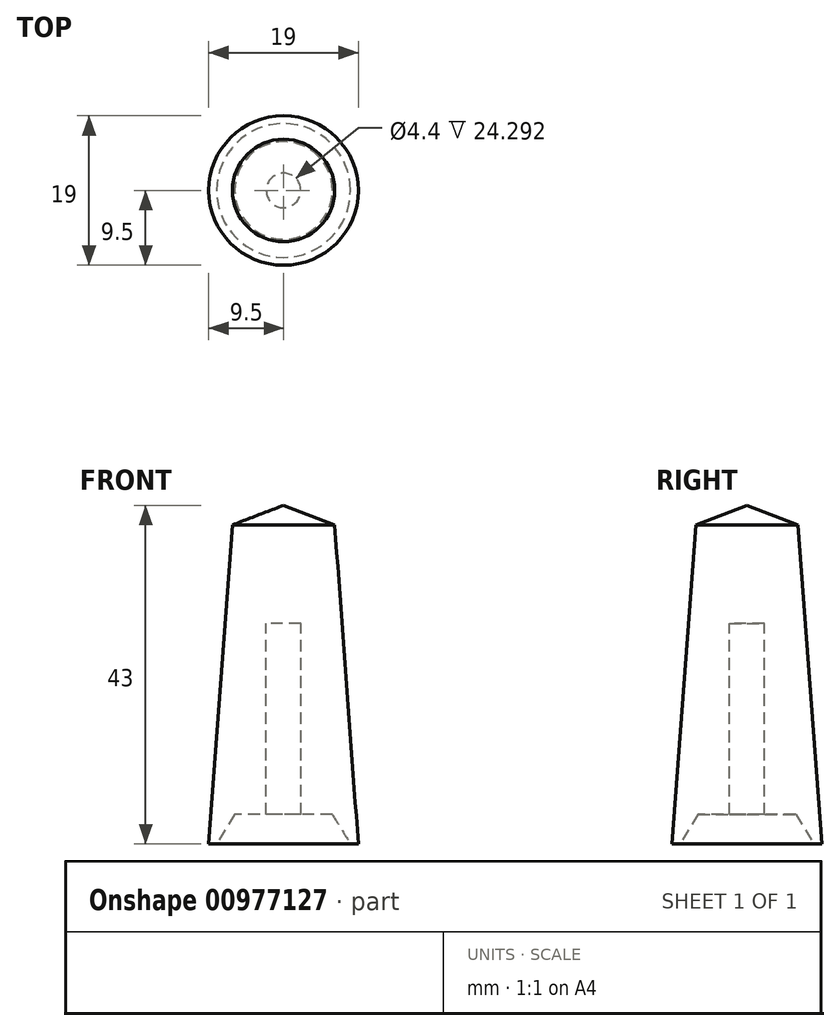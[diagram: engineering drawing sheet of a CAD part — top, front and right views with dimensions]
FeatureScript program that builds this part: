
annotation { "Feature Type Name" : "Feature", "Feature Type Description" : "" }
export const myFeature = defineFeature(function(context is Context, id is Id, definition is map)
    precondition{}
    {
        {
            var Q0;
            Q0=qCreatedBy(makeId("Right.planeOp"),FACE);
            var sketch = newSketch(context, id + "F0", { "sketchPlane" : qUnion([Q0])});
            skLineSegment(sketch, "E0", {"start": v(-8.5, 18.6) * mm, "end": v(-8.5, 3.6) * mm});
            skLineSegment(sketch, "E1", {"start": v(-8.5, 3.6) * mm, "end": v(-6.3, 3.6) * mm});
            skLineSegment(sketch, "E2", {"start": v(-6.3, 3.6) * mm, "end": v(-6.3, -20.7) * mm});
            skLineSegment(sketch, "E3", {"start": v(-6.3, -20.7) * mm, "end": v(-2.3, -20.7) * mm});
            skLineSegment(sketch, "E4", {"start": v(-2.3, -20.7) * mm, "end": v(0, -24.4) * mm});
            skLineSegment(sketch, "E5", {"start": v(0, -24.4) * mm, "end": v(1, -24.4) * mm});
            skLineSegment(sketch, "E6", {"start": v(1, -24.4) * mm, "end": v(-2, 16.1) * mm});
            skLineSegment(sketch, "E7", {"start": v(-2, 16.1) * mm, "end": v(-8.5, 18.6) * mm});
            skSolve(sketch);
        }
        {
            var Q0;
            Q0=makeQuery(id+"F0.imprint","IMPRINT",FACE,{"disambiguationData":[TD([[makeQuery(id+"F0.imprint","IMPRINT",EDGE,{"derivedFrom":sQuery(id+"F0.wireOp",EDGE,"E0")}),1.0]])]});
            var Q1;
            Q1=sQuery(id+"F0.wireOp",EDGE,"E0");
            revolve(context, id + "F1", {"surfaceOperationType" : NewSurfaceOperationType.NEW, "entities" : qUnion([Q0]), "axis" : qUnion([Q1]), "revolveType" : RevolveType.FULL});
        }
    });
